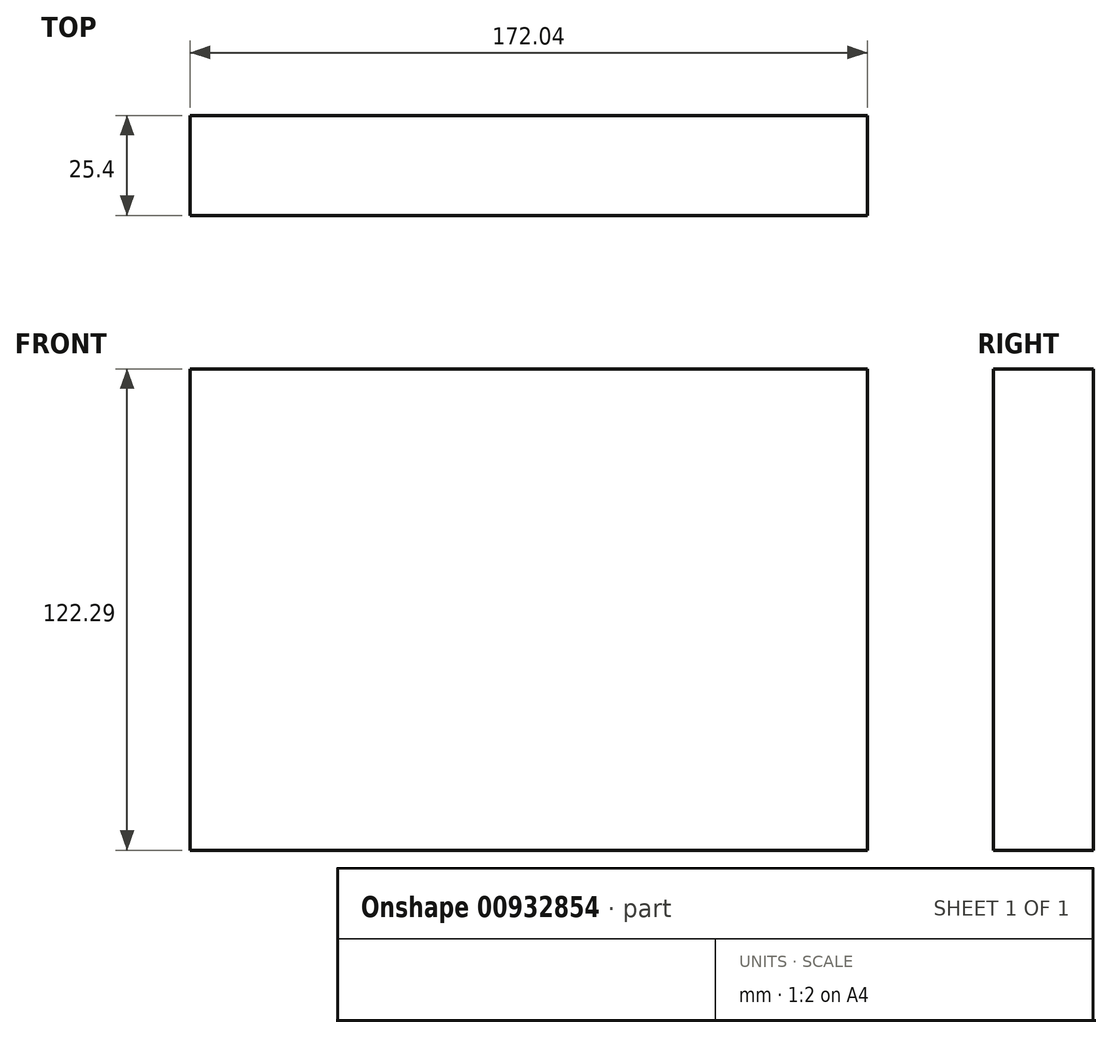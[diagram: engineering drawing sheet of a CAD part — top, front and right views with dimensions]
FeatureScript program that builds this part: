
annotation { "Feature Type Name" : "Feature", "Feature Type Description" : "" }
export const myFeature = defineFeature(function(context is Context, id is Id, definition is map)
    precondition{}
    {
        {
            var Q0;
            Q0=qCreatedBy(makeId("Front.planeOp"),FACE);
            var sketch = newSketch(context, id + "F0", { "sketchPlane" : qUnion([Q0])});
            skLineSegment(sketch, "E0", {"start": v(-64.72, 59.41) * mm, "end": v(107.32, 59.41) * mm});
            skLineSegment(sketch, "E1", {"start": v(107.32, 59.41) * mm, "end": v(107.32, -62.88) * mm});
            skLineSegment(sketch, "E2", {"start": v(107.32, -62.88) * mm, "end": v(-64.72, -62.88) * mm});
            skLineSegment(sketch, "E3", {"start": v(-64.72, -62.88) * mm, "end": v(-64.72, 59.41) * mm});
            skSolve(sketch);
        }
        {
            var Q0;
            Q0 = qSketchRegion(id + "F0", true);
            extrude(context, id + "F1", {"entities" : qUnion([Q0]), "depth" : 25.4 * mm, "offsetDistance" : 25.4 * mm});
        }
    });
